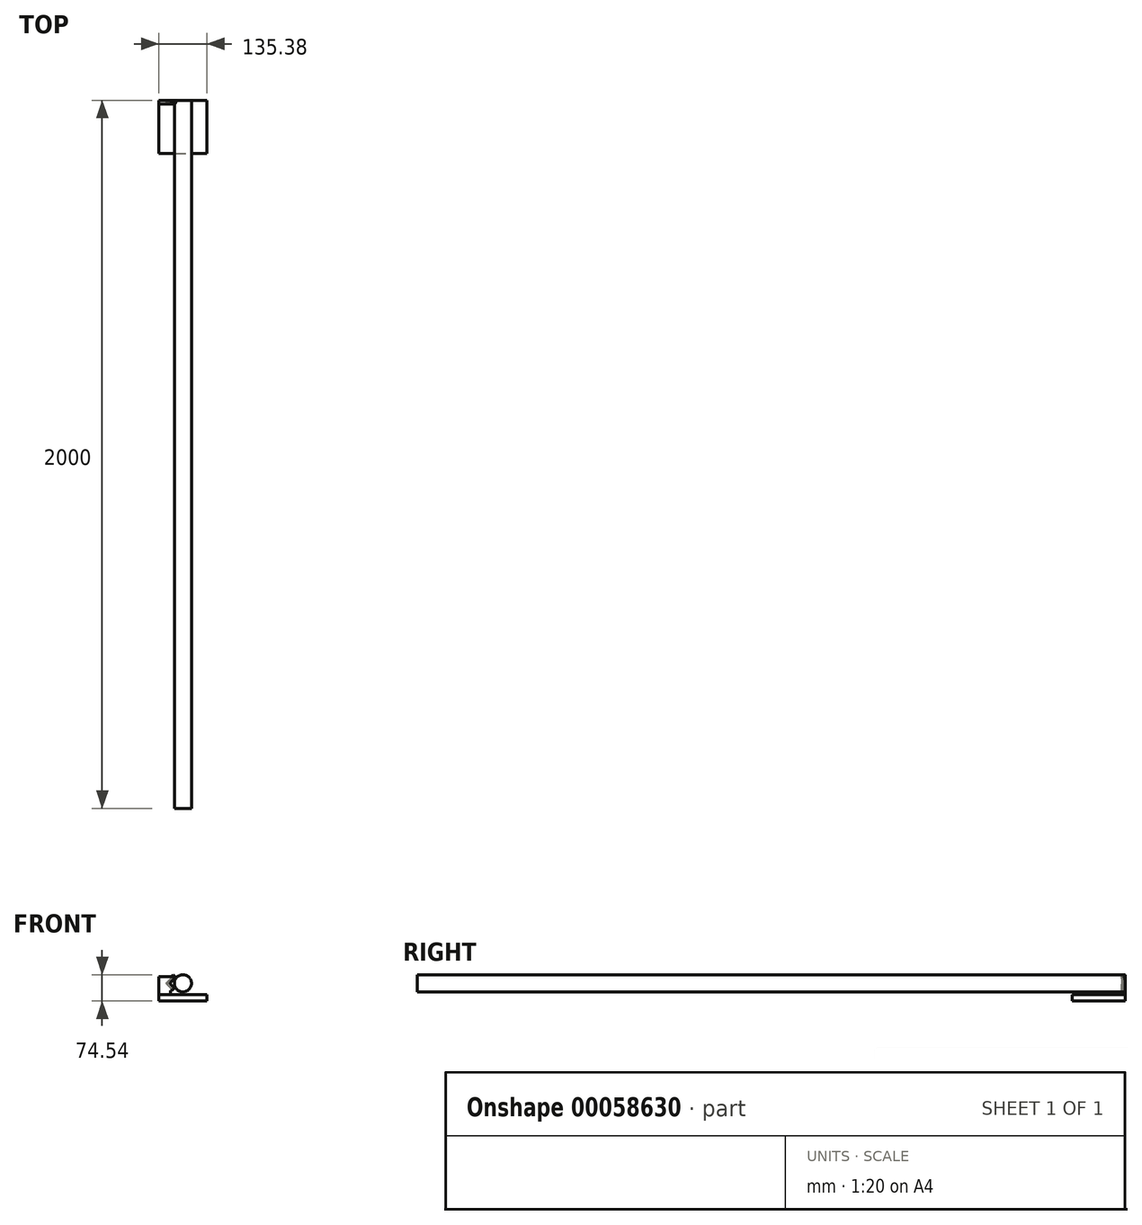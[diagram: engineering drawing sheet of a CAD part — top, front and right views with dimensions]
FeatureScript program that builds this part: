
annotation { "Feature Type Name" : "Feature", "Feature Type Description" : "" }
export const myFeature = defineFeature(function(context is Context, id is Id, definition is map)
    precondition{}
    {
        {
            var Q0;
            Q0=qCreatedBy(makeId("Front.planeOp"),FACE);
            var sketch = newSketch(context, id + "F0", { "sketchPlane" : qUnion([Q0])});
            skLineSegment(sketch, "E0", {"start": v(-90.5, -32.3) * mm, "end": v(85.9, -32.3) * mm, "construction": true});
            skLineSegment(sketch, "E1", {"start": v(0, 0) * mm, "end": v(64.73, 0) * mm, "construction": true});
            skLineSegment(sketch, "E2.2.0", {"start": v(0, 0) * mm, "end": v(0, 64.73) * mm, "construction": true});
            skLineSegment(sketch, "E2.4.0", {"start": v(0, 0) * mm, "end": v(-64.73, 0) * mm, "construction": true});
            skLineSegment(sketch, "E2.6.0", {"start": v(0, 0) * mm, "end": v(0, -64.73) * mm, "construction": true});
            skLineSegment(sketch, "E2.7.0", {"start": v(0, 0) * mm, "end": v(45.77, -45.77) * mm, "construction": true});
            skPoint(sketch, "E3", {"position": v(17.18, -17.18) * mm});
            skLineSegment(sketch, "E4", {"start": v(23.9, -20.36) * mm, "end": v(20.36, -23.9) * mm, "construction": true});
            skPoint(sketch, "E5", {"position": v(22.13, -22.13) * mm});
            skLineSegment(sketch, "E6", {"start": v(18.95, -15.41) * mm, "end": v(15.41, -18.95) * mm, "construction": true});
            skLineSegment(sketch, "E7", {"start": v(18.95, -15.41) * mm, "end": v(28.85, -25.31) * mm, "construction": true});
            skCircle(sketch, "E8", {"center": v(0, 0) * mm, "radius": 24.3 * mm});
            skLineSegment(sketch, "E9.MirrorCS", {"start": v(15.41, -18.95) * mm, "end": v(25.31, -28.85) * mm, "construction": true});
            skLineSegment(sketch, "E10.MirrorCS", {"start": v(28.85, -25.31) * mm, "end": v(25.31, -28.85) * mm, "construction": true});
            skLineSegment(sketch, "E11", {"start": v(18.95, -15.41) * mm, "end": v(28.85, -25.31) * mm});
            skLineSegment(sketch, "E12", {"start": v(28.85, -25.31) * mm, "end": v(25.31, -28.85) * mm});
            skLineSegment(sketch, "E13", {"start": v(25.31, -28.85) * mm, "end": v(15.41, -18.95) * mm});
            skLineSegment(sketch, "E14", {"start": v(15.41, -18.95) * mm, "end": v(18.95, -15.41) * mm});
            skLineSegment(sketch, "E15", {"start": v(-35, -32.3) * mm, "end": v(-67.7, -32.3) * mm});
            skPoint(sketch, "E16", {"position": v(0, -32.3) * mm});
            skLineSegment(sketch, "E17", {"start": v(22.13, -18.6) * mm, "end": v(18.6, -22.13) * mm, "construction": true});
            skLineSegment(sketch, "E18.MirrorCS", {"start": v(25.67, -22.13) * mm, "end": v(22.13, -25.67) * mm, "construction": true});
            skLineSegment(sketch, "E19.1.0", {"start": v(15.41, 18.95) * mm, "end": v(25.31, 28.85) * mm});
            skPoint(sketch, "E19.1.1", {"position": v(22.13, 22.13) * mm});
            skLineSegment(sketch, "E19.1.2", {"start": v(28.85, 25.31) * mm, "end": v(18.95, 15.41) * mm});
            skLineSegment(sketch, "E19.1.3", {"start": v(22.13, 25.67) * mm, "end": v(25.67, 22.13) * mm, "construction": true});
            skPoint(sketch, "E19.1.4", {"position": v(17.18, 17.18) * mm});
            skLineSegment(sketch, "E19.1.5", {"start": v(18.6, 22.13) * mm, "end": v(22.13, 18.6) * mm, "construction": true});
            skLineSegment(sketch, "E19.1.6", {"start": v(25.31, 28.85) * mm, "end": v(28.85, 25.31) * mm});
            skLineSegment(sketch, "E19.1.7", {"start": v(0, 0) * mm, "end": v(45.77, 45.77) * mm, "construction": true});
            skLineSegment(sketch, "E19.1.8", {"start": v(18.95, 15.41) * mm, "end": v(15.41, 18.95) * mm});
            skLineSegment(sketch, "E19.1.9", {"start": v(20.36, 23.9) * mm, "end": v(23.9, 20.36) * mm, "construction": true});
            skLineSegment(sketch, "E19.1.10", {"start": v(15.41, 18.95) * mm, "end": v(25.31, 28.85) * mm, "construction": true});
            skLineSegment(sketch, "E19.1.11", {"start": v(18.95, 15.41) * mm, "end": v(28.85, 25.31) * mm, "construction": true});
            skLineSegment(sketch, "E19.1.12", {"start": v(25.31, 28.85) * mm, "end": v(28.85, 25.31) * mm, "construction": true});
            skLineSegment(sketch, "E19.1.13", {"start": v(15.41, 18.95) * mm, "end": v(18.95, 15.41) * mm, "construction": true});
            skLineSegment(sketch, "E19.2.0", {"start": v(-18.95, 15.41) * mm, "end": v(-28.85, 25.31) * mm});
            skPoint(sketch, "E19.2.1", {"position": v(-22.13, 22.13) * mm});
            skLineSegment(sketch, "E19.2.2", {"start": v(-25.31, 28.85) * mm, "end": v(-15.41, 18.95) * mm});
            skLineSegment(sketch, "E19.2.3", {"start": v(-25.67, 22.13) * mm, "end": v(-22.13, 25.67) * mm, "construction": true});
            skPoint(sketch, "E19.2.4", {"position": v(-17.18, 17.18) * mm});
            skLineSegment(sketch, "E19.2.5", {"start": v(-22.13, 18.6) * mm, "end": v(-18.6, 22.13) * mm, "construction": true});
            skLineSegment(sketch, "E19.2.6", {"start": v(-28.85, 25.31) * mm, "end": v(-25.31, 28.85) * mm});
            skLineSegment(sketch, "E19.2.7", {"start": v(0, 0) * mm, "end": v(-45.77, 45.77) * mm, "construction": true});
            skLineSegment(sketch, "E19.2.8", {"start": v(-15.41, 18.95) * mm, "end": v(-18.95, 15.41) * mm});
            skLineSegment(sketch, "E19.2.9", {"start": v(-23.9, 20.36) * mm, "end": v(-20.36, 23.9) * mm, "construction": true});
            skLineSegment(sketch, "E19.2.10", {"start": v(-18.95, 15.41) * mm, "end": v(-28.85, 25.31) * mm, "construction": true});
            skLineSegment(sketch, "E19.2.11", {"start": v(-15.41, 18.95) * mm, "end": v(-25.31, 28.85) * mm, "construction": true});
            skLineSegment(sketch, "E19.2.12", {"start": v(-28.85, 25.31) * mm, "end": v(-25.31, 28.85) * mm, "construction": true});
            skLineSegment(sketch, "E19.2.13", {"start": v(-18.95, 15.41) * mm, "end": v(-15.41, 18.95) * mm, "construction": true});
            skLineSegment(sketch, "E19.3.0", {"start": v(-15.41, -18.95) * mm, "end": v(-25.31, -28.85) * mm});
            skPoint(sketch, "E19.3.1", {"position": v(-22.13, -22.13) * mm});
            skLineSegment(sketch, "E19.3.2", {"start": v(-28.85, -25.31) * mm, "end": v(-18.95, -15.41) * mm});
            skLineSegment(sketch, "E19.3.3", {"start": v(-22.13, -25.67) * mm, "end": v(-25.67, -22.13) * mm, "construction": true});
            skPoint(sketch, "E19.3.4", {"position": v(-17.18, -17.18) * mm});
            skLineSegment(sketch, "E19.3.5", {"start": v(-18.6, -22.13) * mm, "end": v(-22.13, -18.6) * mm, "construction": true});
            skLineSegment(sketch, "E19.3.6", {"start": v(-25.31, -28.85) * mm, "end": v(-28.85, -25.31) * mm});
            skLineSegment(sketch, "E19.3.7", {"start": v(0, 0) * mm, "end": v(-45.77, -45.77) * mm, "construction": true});
            skLineSegment(sketch, "E19.3.8", {"start": v(-18.95, -15.41) * mm, "end": v(-15.41, -18.95) * mm});
            skLineSegment(sketch, "E19.3.9", {"start": v(-20.36, -23.9) * mm, "end": v(-23.9, -20.36) * mm, "construction": true});
            skLineSegment(sketch, "E19.3.10", {"start": v(-15.41, -18.95) * mm, "end": v(-25.31, -28.85) * mm, "construction": true});
            skLineSegment(sketch, "E19.3.11", {"start": v(-18.95, -15.41) * mm, "end": v(-28.85, -25.31) * mm, "construction": true});
            skLineSegment(sketch, "E19.3.12", {"start": v(-25.31, -28.85) * mm, "end": v(-28.85, -25.31) * mm, "construction": true});
            skLineSegment(sketch, "E19.3.13", {"start": v(-15.41, -18.95) * mm, "end": v(-18.95, -15.41) * mm, "construction": true});
            skLineSegment(sketch, "E20", {"start": v(-67.7, -32.3) * mm, "end": v(-67.7, 18.98) * mm});
            skLineSegment(sketch, "E21", {"start": v(-67.7, 18.98) * mm, "end": v(-35, 18.98) * mm});
            skLineSegment(sketch, "E22", {"start": v(-35, 18.98) * mm, "end": v(-35, -32.3) * mm});
            skLineSegment(sketch, "E23", {"start": v(-30.97, 20.36) * mm, "end": v(-23.9, 13.3) * mm});
            skLineSegment(sketch, "E24", {"start": v(-30.97, 20.36) * mm, "end": v(-35, 16.34) * mm});
            skLineSegment(sketch, "E25", {"start": v(-23.9, 13.3) * mm, "end": v(-35, 2.2) * mm});
            skLineSegment(sketch, "E26", {"start": v(-23.9, 20.36) * mm, "end": v(-29.45, 14.81) * mm, "construction": true});
            skPoint(sketch, "E26.endSnap0", {"position": v(-29.45, 7.74) * mm});
            skPoint(sketch, "E27", {"position": v(-27.44, 16.83) * mm});
            skLineSegment(sketch, "E28.MirrorCS", {"start": v(-30.97, -20.36) * mm, "end": v(-23.9, -13.3) * mm});
            skLineSegment(sketch, "E29.MirrorCS", {"start": v(-30.97, -20.36) * mm, "end": v(-35, -16.34) * mm});
            skLineSegment(sketch, "E30.MirrorCS", {"start": v(-23.9, -13.3) * mm, "end": v(-35, -2.2) * mm});
            skLineSegment(sketch, "E31", {"start": v(-30.97, -20.36) * mm, "end": v(-35, -20.36) * mm});
            skLineSegment(sketch, "E32", {"start": v(-35, 18.98) * mm, "end": v(-32.36, 18.98) * mm});
            skLineSegment(sketch, "E33.bottom", {"start": v(-67.7, -32.3) * mm, "end": v(0, -32.3) * mm});
            skLineSegment(sketch, "E33.top", {"start": v(-67.7, -50.24) * mm, "end": v(0, -50.24) * mm});
            skLineSegment(sketch, "E33.left", {"start": v(-67.7, -32.3) * mm, "end": v(-67.7, -50.24) * mm});
            skLineSegment(sketch, "E33.right", {"start": v(0, -32.3) * mm, "end": v(0, -50.24) * mm});
            skLineSegment(sketch, "E34", {"start": v(-30.97, 20.36) * mm, "end": v(-27.44, 23.9) * mm});
            skLineSegment(sketch, "E35", {"start": v(-23.9, 13.3) * mm, "end": v(-20.36, 16.83) * mm});
            skSolve(sketch);
        }
        {
            var Q0;
            {var subQ0=sQuery(id+"F0.wireOp",EDGE,"E8");var subQ1=makeQuery(id+"F0.imprint","INTERSECT",VERTEX,{"derivedFrom":[subQ0,sQuery(id+"F0.wireOp",EDGE,"79785924-a6a1-45ce-891b-6658fc673912.2.2")]});Q0=makeQuery(id+"F0.imprint","IMPRINT",FACE,{"disambiguationData":[TD([[makeQuery(id+"F0.imprint","IMPRINT",EDGE,{"disambiguationData":[TD([[subQ1,1.0]])],"derivedFrom":subQ0}),1.0]])]});}
            extrude(context, id + "F1", {"entities" : qUnion([Q0]), "depth" : 2000 * mm});
        }
        {
            var Q0;
            {var subQ4=sQuery(id+"F0.wireOp",EDGE,"E23");Q0=makeQuery(id+"F0.imprint","IMPRINT",FACE,{"disambiguationData":[TD([[makeQuery(id+"F0.imprint","IMPRINT",EDGE,{"derivedFrom":subQ4}),-1.0]])]});}
            var Q1;
            {var subQ0=sQuery(id+"F0.wireOp",EDGE,"E32");Q1=makeQuery(id+"F0.imprint","IMPRINT",FACE,{"disambiguationData":[TD([[makeQuery(id+"F0.imprint","IMPRINT",EDGE,{"derivedFrom":subQ0}),-1.0]])]});}
            var Q2;
            {var subQ4=sQuery(id+"F0.wireOp",EDGE,"E20");Q2=makeQuery(id+"F0.imprint","IMPRINT",FACE,{"disambiguationData":[TD([[makeQuery(id+"F0.imprint","IMPRINT",EDGE,{"derivedFrom":subQ4}),-1.0]])]});}
            var Q3;
            Q3=makeQuery(id+"F0.imprint","IMPRINT",FACE,{"disambiguationData":[TD([[makeQuery(id+"F0.imprint","IMPRINT",EDGE,{"derivedFrom":sQuery(id+"F0.wireOp",EDGE,"E28.MirrorCS")}),1.0]])]});
            var Q4;
            {var subQ0=sQuery(id+"F0.wireOp",EDGE,"E29.MirrorCS");Q4=makeQuery(id+"F0.imprint","IMPRINT",FACE,{"disambiguationData":[TD([[makeQuery(id+"F0.imprint","IMPRINT",EDGE,{"derivedFrom":subQ0}),1.0]])]});}
            extrude(context, id + "F2", {"entities" : qUnion([Q0, Q1, Q2, Q3, Q4]), "depth" : 10 * mm});
        }
        {
            var Q0;
            Q0=makeQuery(id+"F2.opExtrude","SWEPT_FACE",FACE,{"disambiguationData":[OSD([sQuery(id+"F0.wireOp",EDGE,"E23")])]});
            var sketch = newSketch(context, id + "F3", { "sketchPlane" : qUnion([Q0])});
            skLineSegment(sketch, "E36", {"start": v(-5, 36.3) * mm, "end": v(-5, 26.3) * mm, "construction": true});
            skCircle(sketch, "E37", {"center": v(-5, 31.3) * mm, "radius": 2.5 * mm});
            skSolve(sketch);
        }
        {
            var Q0;
            Q0=makeQuery(id+"F3.imprint","IMPRINT",FACE,{"disambiguationData":[TD([[makeQuery(id+"F3.imprint","IMPRINT",EDGE,{"derivedFrom":sQuery(id+"F3.wireOp",EDGE,"E37")}),1.0]])]});
            extrude(context, id + "F4", {"entities" : qUnion([Q0]), "operationType" : NewBodyOperationType.REMOVE, "oppositeDirection" : true, "depth" : 25 * mm});
        }
        {
            var Q0;
            Q0=makeQuery(id+"F2.opExtrude","SWEPT_FACE",FACE,{"disambiguationData":[OSD([sQuery(id+"F0.wireOp",EDGE,"E28.MirrorCS")])]});
            var sketch = newSketch(context, id + "F5", { "sketchPlane" : qUnion([Q0])});
            skLineSegment(sketch, "E38", {"start": v(-5, -26.3) * mm, "end": v(-5, -36.3) * mm, "construction": true});
            skCircle(sketch, "E39", {"center": v(-5, -31.3) * mm, "radius": 2.5 * mm});
            skSolve(sketch);
        }
        {
            var Q0;
            Q0=makeQuery(id+"F5.imprint","IMPRINT",FACE,{"disambiguationData":[TD([[makeQuery(id+"F5.imprint","IMPRINT",EDGE,{"derivedFrom":sQuery(id+"F5.wireOp",EDGE,"E39")}),1.0]])]});
            extrude(context, id + "F6", {"entities" : qUnion([Q0]), "operationType" : NewBodyOperationType.REMOVE, "oppositeDirection" : true, "depth" : 25 * mm});
        }
        {
            var Q0;
            Q0=makeQuery(id+"F0.imprint","IMPRINT",FACE,{"disambiguationData":[TD([[makeQuery(id+"F0.imprint","IMPRINT",EDGE,{"derivedFrom":sQuery(id+"F0.wireOp",EDGE,"E33.top")}),1.0]])]});
            extrude(context, id + "F7", {"entities" : qUnion([Q0]), "depth" : 150 * mm});
        }
        {
            var Q0;
            Q0=makeQuery(id+"F7.opExtrude","SWEPT_BODY",BODY,{"disambiguationData":[OSD([sQuery(id+"F0.wireOp",EDGE,"E33.bottom"),sQuery(id+"F0.wireOp",EDGE,"E33.top"),sQuery(id+"F0.wireOp",EDGE,"E33.left"),sQuery(id+"F0.wireOp",EDGE,"E33.right")])]});
            var Q1;
            Q1=makeQuery(id+"F7.opExtrude","SWEPT_FACE",FACE,{"disambiguationData":[OSD([sQuery(id+"F0.wireOp",EDGE,"E33.right")])]});
            mirror(context, id + "F8", {"operationType" : NewBodyOperationType.ADD, "entities" : qUnion([Q0]), "mirrorPlane" : qUnion([Q1])});
        }
        {
            var Q0;
            Q0=makeQuery(id+"F0.imprint","IMPRINT",FACE,{"disambiguationData":[TD([[makeQuery(id+"F0.imprint","IMPRINT",EDGE,{"derivedFrom":sQuery(id+"F0.wireOp",EDGE,"E23")}),1.0]])]});
            extrude(context, id + "F9", {"entities" : qUnion([Q0]), "depth" : 10 * mm});
        }
        {
            var Q0;
            Q0=makeQuery(id+"F3.imprint","IMPRINT",FACE,{"disambiguationData":[TD([[makeQuery(id+"F3.imprint","IMPRINT",EDGE,{"derivedFrom":sQuery(id+"F3.wireOp",EDGE,"E37")}),1.0]])]});
            extrude(context, id + "F10", {"entities" : qUnion([Q0]), "operationType" : NewBodyOperationType.REMOVE, "depth" : 25 * mm});
        }
        {
            var Q0;
            Q0=makeQuery(id+"F9.opExtrude","CAP_EDGE",EDGE,{"disambiguationData":[OSD([sQuery(id+"F0.wireOp",EDGE,"E34")])],"isStart":true});
            var Q1;
            Q1=makeQuery(id+"F9.opExtrude","CAP_EDGE",EDGE,{"disambiguationData":[OSD([sQuery(id+"F0.wireOp",EDGE,"E34")])],"isStart":false});
            var Q2;
            Q2=makeQuery(id+"F9.opExtrude","CAP_EDGE",EDGE,{"disambiguationData":[OSD([sQuery(id+"F0.wireOp",EDGE,"E35")])],"isStart":false});
            var Q3;
            Q3=makeQuery(id+"F9.opExtrude","CAP_EDGE",EDGE,{"disambiguationData":[OSD([sQuery(id+"F0.wireOp",EDGE,"E35")])],"isStart":true});
            fillet(context, id + "F11", {"entities" : qUnion([Q0, Q1, Q2, Q3]), "radius" : 5 * mm, "tangentPropagation" : true, "allowEdgeOverflow" : false});
        }
    });
